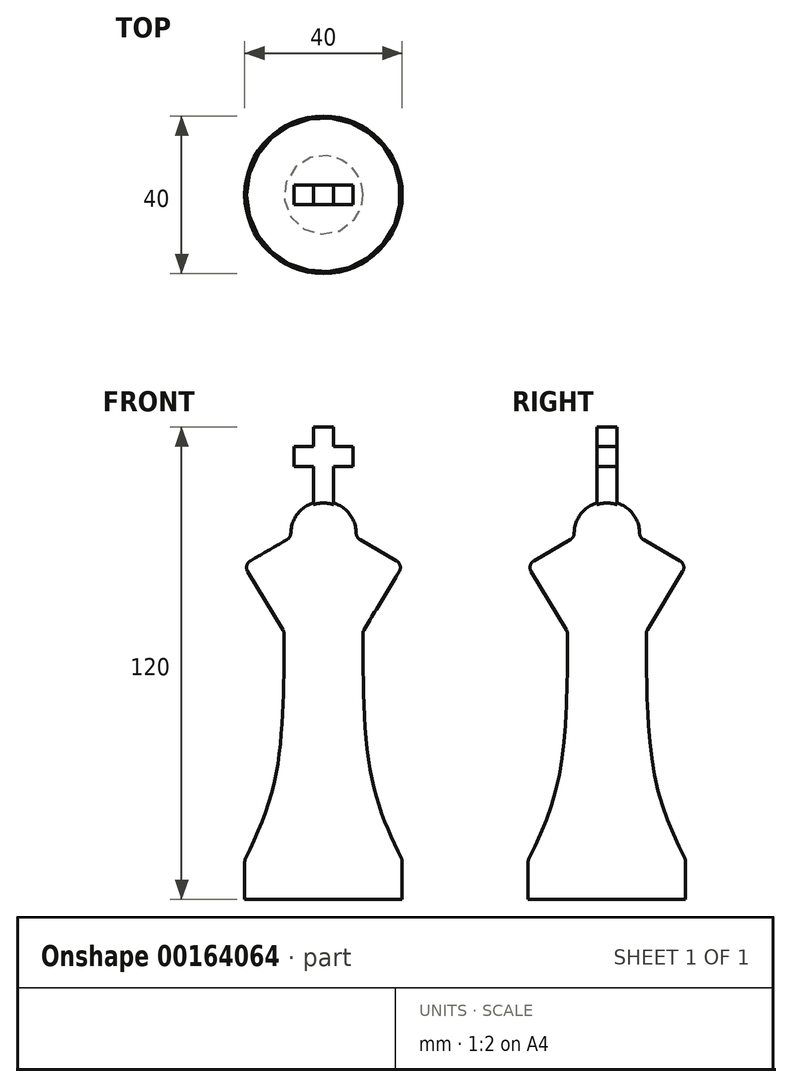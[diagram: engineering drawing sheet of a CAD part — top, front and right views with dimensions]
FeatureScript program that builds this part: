
annotation { "Feature Type Name" : "Feature", "Feature Type Description" : "" }
export const myFeature = defineFeature(function(context is Context, id is Id, definition is map)
    precondition{}
    {
        {
            var Q0;
            Q0=qCreatedBy(makeId("Front.planeOp"),FACE);
            var sketch = newSketch(context, id + "F0", { "sketchPlane" : qUnion([Q0])});
            skLineSegment(sketch, "E0.bottom", {"start": v(-2.5, 120) * mm, "end": v(2.5, 120) * mm});
            skLineSegment(sketch, "E0.top", {"start": v(-2.5, 100) * mm, "end": v(2.5, 100) * mm});
            skLineSegment(sketch, "E0.left", {"start": v(-2.5, 120) * mm, "end": v(-2.5, 100) * mm});
            skLineSegment(sketch, "E0.right", {"start": v(2.5, 120) * mm, "end": v(2.5, 100) * mm});
            skSolve(sketch);
        }
        {
            var Q0;
            Q0 = qSketchRegion(id + "F0", true);
            var Q1;
            Q1=makeQuery(id+"F0.imprint","IMPRINT",FACE,{"disambiguationData":[TD([[makeQuery(id+"F0.imprint","IMPRINT",EDGE,{"derivedFrom":sQuery(id+"F0.wireOp",EDGE,"E0.bottom")}),-1.0]])]});
            extrude(context, id + "F1", {"entities" : qUnion([Q0, Q1]), "depth" : 2.5 * mm});
        }
        {
            var Q0;
            Q0=makeQuery(id+"F1.opExtrude","CAP_FACE",FACE,{"disambiguationData":[OSD([sQuery(id+"F0.wireOp",EDGE,"E0.bottom"),sQuery(id+"F0.wireOp",EDGE,"E0.top"),sQuery(id+"F0.wireOp",EDGE,"E0.left"),sQuery(id+"F0.wireOp",EDGE,"E0.right")])],"isStart":false});
            var sketch = newSketch(context, id + "F2", { "sketchPlane" : qUnion([Q0])});
            skLineSegment(sketch, "E1.bottom", {"start": v(-7.5, 115) * mm, "end": v(7.5, 115) * mm});
            skLineSegment(sketch, "E1.top", {"start": v(-7.5, 110) * mm, "end": v(7.5, 110) * mm});
            skLineSegment(sketch, "E1.left", {"start": v(-7.5, 115) * mm, "end": v(-7.5, 110) * mm});
            skLineSegment(sketch, "E1.right", {"start": v(7.5, 115) * mm, "end": v(7.5, 110) * mm});
            skSolve(sketch);
        }
        {
            var Q0;
            Q0 = qSketchRegion(id + "F2", true);
            extrude(context, id + "F3", {"entities" : qUnion([Q0]), "operationType" : NewBodyOperationType.ADD, "oppositeDirection" : true, "depth" : 2.5 * mm});
        }
        {
            var Q0;
            Q0=qCreatedBy(makeId("Front.planeOp"),FACE);
            var sketch = newSketch(context, id + "F4", { "sketchPlane" : qUnion([Q0])});
            skLineSegment(sketch, "E2", {"start": v(-8.24, 92) * mm, "end": v(-20.3, 85) * mm});
            skLineSegment(sketch, "E3", {"start": v(-20.3, 85) * mm, "end": v(-10, 68) * mm});
            skLineSegment(sketch, "E4", {"start": v(-20, 10) * mm, "end": v(-20, 0) * mm});
            skLineSegment(sketch, "E5", {"start": v(-20, 0) * mm, "end": v(0, 0) * mm});
            skArc(sketch, "E6", {"start": v(0, 101) * mm, "mid": v(-6.2, 98.4) * mm, "end": v(-8.24, 92) * mm});
            skLineSegment(sketch, "E7", {"start": v(0, 101) * mm, "end": v(0, 0) * mm});
            skFitSpline(sketch, "E8", {"points": [v(-10, 68) * mm, v(-12.34, 30.38) * mm, v(-20, 10) * mm], "startDerivative": vector(-0.24, -71.61) * mm, "endDerivative": vector(-20.69, -43.1) * mm});
            skSolve(sketch);
        }
        {
            var Q0;
            Q0 = qSketchRegion(id + "F4", true);
            var Q1;
            Q1=sQuery(id+"F4.wireOp",EDGE,"E7");
            revolve(context, id + "F5", {"operationType" : NewBodyOperationType.ADD, "entities" : qUnion([Q0]), "axis" : qUnion([Q1]), "revolveType" : RevolveType.FULL});
        }
        {
            var Q0;
            Q0 = qSketchRegion(id + "F0", true);
            extrude(context, id + "F6", {"entities" : qUnion([Q0]), "operationType" : NewBodyOperationType.ADD, "oppositeDirection" : true, "depth" : 2.5 * mm});
        }
        {
            var Q0;
            Q0 = qSketchRegion(id + "F2", true);
            extrude(context, id + "F7", {"entities" : qUnion([Q0]), "operationType" : NewBodyOperationType.ADD, "oppositeDirection" : true, "depth" : 5 * mm});
        }
        {
            var Q0;
            Q0=makeQuery(id+"F5.opRevolve","SWEPT_EDGE",EDGE,{"disambiguationData":[OSD([sQuery(id+"F4.wireOp",EDGE,"E2"),sQuery(id+"F4.wireOp",EDGE,"E3")])]});
            var Q1;
            Q1=makeQuery(id+"F5.opRevolve","SWEPT_EDGE",EDGE,{"disambiguationData":[OSD([sQuery(id+"F4.wireOp",EDGE,"E4"),sQuery(id+"F4.wireOp",EDGE,"E8")])]});
            var Q2;
            Q2=makeQuery(id+"F5.opRevolve","SWEPT_EDGE",EDGE,{"disambiguationData":[OSD([sQuery(id+"F4.wireOp",EDGE,"E3"),sQuery(id+"F4.wireOp",EDGE,"E8")])]});
            var Q3;
            Q3=makeQuery(id+"F5.opRevolve","SWEPT_EDGE",EDGE,{"disambiguationData":[OSD([sQuery(id+"F4.wireOp",EDGE,"E2"),sQuery(id+"F4.wireOp",EDGE,"E6")])]});
            fillet(context, id + "F8", {"entities" : qUnion([Q0, Q1, Q2, Q3]), "radius" : 2 * mm, "tangentPropagation" : true, "allowEdgeOverflow" : false});
        }
    });
